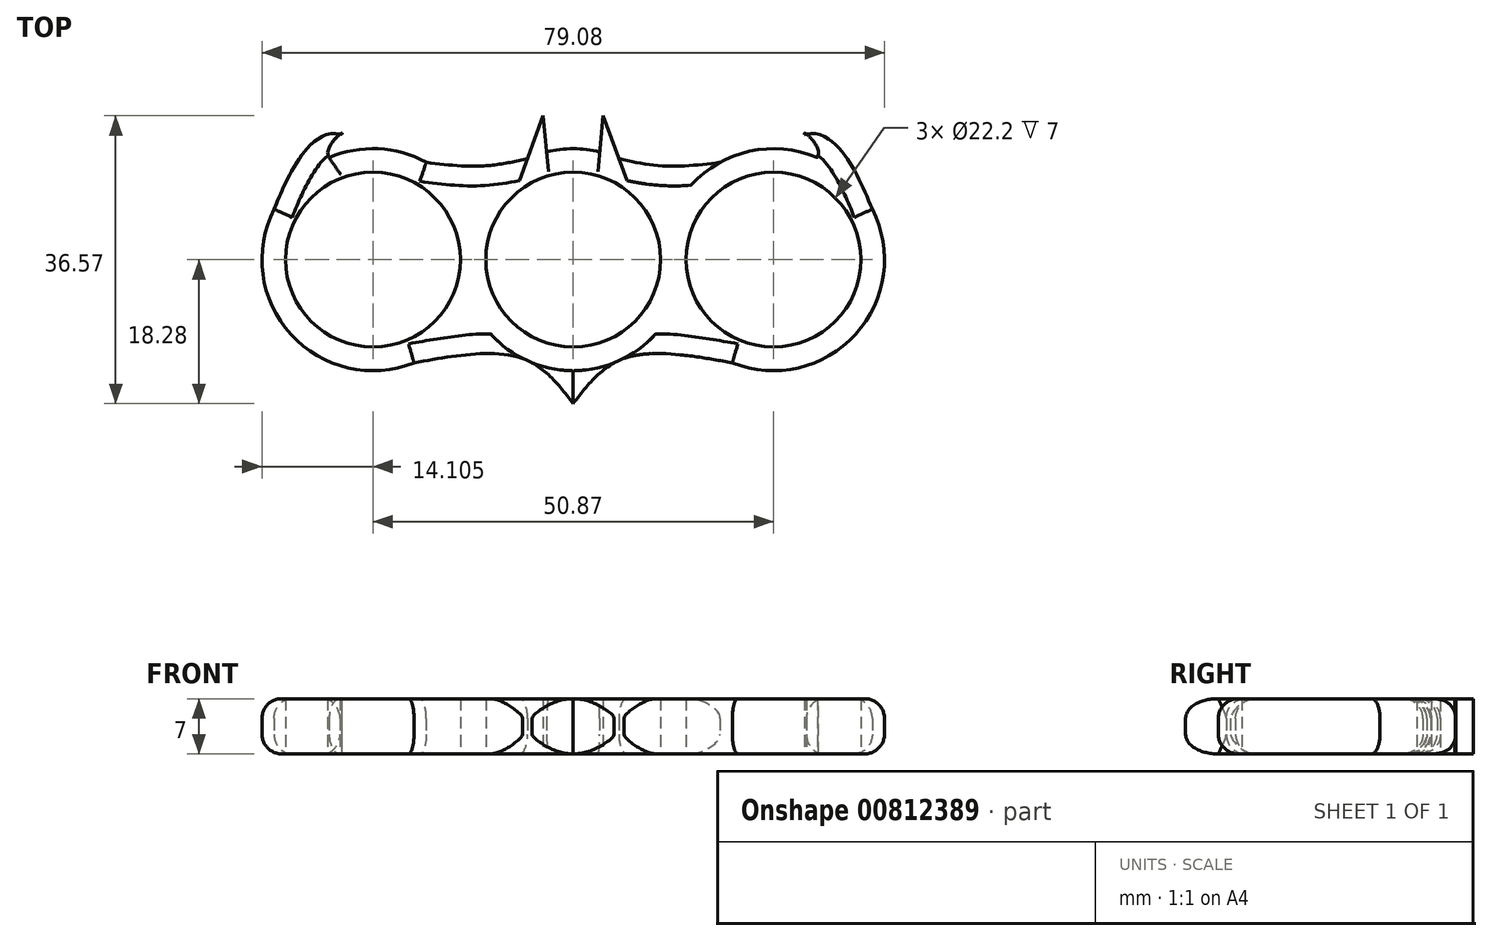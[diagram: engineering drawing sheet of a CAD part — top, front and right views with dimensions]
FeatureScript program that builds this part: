
annotation { "Feature Type Name" : "Feature", "Feature Type Description" : "" }
export const myFeature = defineFeature(function(context is Context, id is Id, definition is map)
    precondition{}
    {
        {
            var Q0;
            Q0=qCreatedBy(makeId("Top.planeOp"),FACE);
            var sketch = newSketch(context, id + "F0", { "sketchPlane" : qUnion([Q0])});
            skCircle(sketch, "E0", {"center": v(0, 0) * mm, "radius": 11.1 * mm});
            skCircle(sketch, "E1", {"center": v(0, 0) * mm, "radius": 14.1 * mm});
            skLineSegment(sketch, "E2", {"start": v(-3.37, 13.7) * mm, "end": v(-3.8, 18.3) * mm});
            skLineSegment(sketch, "E3", {"start": v(-3.8, 18.3) * mm, "end": v(-5.79, 12.86) * mm});
            skCircle(sketch, "E4", {"center": v(-25.44, 0) * mm, "radius": 11.1 * mm});
            skCircle(sketch, "E5", {"center": v(-25.44, 0) * mm, "radius": 14.1 * mm});
            skFitSpline(sketch, "E6", {"points": [v(-5.79, 12.86) * mm, v(-18.67, 12.37) * mm], "startDerivative": vector(-16.12, -4.1) * mm, "endDerivative": vector(-14.26, 1.86) * mm});
            skFitSpline(sketch, "E7", {"points": [v(-31, 12.95) * mm, v(-29.4, 15.9) * mm], "startDerivative": vector(-2.6, 3.82) * mm, "endDerivative": vector(-1.29, -2.38) * mm});
            skFitSpline(sketch, "E8", {"points": [v(-29.4, 15.9) * mm, v(-38.8, 4.5) * mm], "startDerivative": vector(-14.93, 3.99) * mm, "endDerivative": vector(-3.9, -8.33) * mm});
            skFitSpline(sketch, "E9", {"points": [v(-20.22, -13.1) * mm, v(-6.43, -12.55) * mm, v(0, -18.28) * mm], "startDerivative": vector(27.44, 4.82) * mm, "endDerivative": vector(12.4, -15.93) * mm});
            skLineSegment(sketch, "E10", {"start": v(0, 14.1) * mm, "end": v(0, -18.28) * mm, "construction": true});
            skLineSegment(sketch, "E11.MirrorCS", {"start": v(3.8, 18.3) * mm, "end": v(5.79, 12.86) * mm});
            skLineSegment(sketch, "E12.MirrorCS", {"start": v(3.37, 13.7) * mm, "end": v(3.8, 18.3) * mm});
            skFitSpline(sketch, "E13.MirrorCS", {"points": [v(5.79, 12.86) * mm, v(18.67, 12.37) * mm], "startDerivative": vector(16.12, -4.1) * mm, "endDerivative": vector(14.26, 1.86) * mm});
            skCircle(sketch, "E14.MirrorC", {"center": v(25.44, 0) * mm, "radius": 11.1 * mm});
            skCircle(sketch, "E15.MirrorC", {"center": v(25.44, 0) * mm, "radius": 14.1 * mm});
            skFitSpline(sketch, "E16.MirrorCS", {"points": [v(20.22, -13.1) * mm, v(6.43, -12.55) * mm, v(0, -18.28) * mm], "startDerivative": vector(-27.44, 4.82) * mm, "endDerivative": vector(-12.4, -15.93) * mm});
            skFitSpline(sketch, "E17.MirrorCS", {"points": [v(29.4, 15.9) * mm, v(38.8, 4.5) * mm], "startDerivative": vector(14.93, 3.99) * mm, "endDerivative": vector(3.9, -8.33) * mm});
            skFitSpline(sketch, "E18.MirrorCS", {"points": [v(31, 12.95) * mm, v(29.4, 15.9) * mm], "startDerivative": vector(2.6, 3.82) * mm, "endDerivative": vector(1.29, -2.38) * mm});
            skLineSegment(sketch, "E19.MirrorCS", {"start": v(34.7, 6.12) * mm, "end": v(29.4, 15.9) * mm, "construction": true});
            skSolve(sketch);
        }
        {
            var Q0;
            Q0 = qSketchRegion(id + "F0", true);
            var Q1;
            {var subQ0=sQuery(id+"F0.wireOp",EDGE,"E15.MirrorC");var subQ1=sQuery(id+"F0.wireOp",EDGE,"E1");var subQ2=makeQuery(id+"F0.imprint","INTERSECT",VERTEX,{"disambiguationData":[OD(0.0)],"derivedFrom":[subQ1,subQ0]});Q1=makeQuery(id+"F0.imprint","IMPRINT",FACE,{"disambiguationData":[TD([[makeQuery(id+"F0.imprint","IMPRINT",EDGE,{"disambiguationData":[TD([[subQ2,1.0]])],"derivedFrom":subQ1}),1.0]])]});}
            var Q2;
            {var subQ0=sQuery(id+"F0.wireOp",EDGE,"E5");var subQ1=sQuery(id+"F0.wireOp",EDGE,"E1");var subQ2=makeQuery(id+"F0.imprint","INTERSECT",VERTEX,{"disambiguationData":[OD(0.0)],"derivedFrom":[subQ1,subQ0]});Q2=makeQuery(id+"F0.imprint","IMPRINT",FACE,{"disambiguationData":[TD([[makeQuery(id+"F0.imprint","IMPRINT",EDGE,{"disambiguationData":[TD([[subQ2,-1.0]])],"derivedFrom":subQ1}),1.0]])]});}
            extrude(context, id + "F1", {"entities" : qUnion([Q0, Q1, Q2]), "depth" : 7 * mm, "offsetDistance" : 25 * mm});
        }
        {
            var Q0;
            {var subQ0=sQuery(id+"F0.wireOp",EDGE,"E5");Q0=makeQuery(id+"F1.opExtrude","CAP_EDGE",EDGE,{"disambiguationData":[OSD([subQ0]),TDD([makeQuery(id+"F0.imprint","IMPRINT",EDGE,{"disambiguationData":[TD([[makeQuery(id+"F0.imprint","INTERSECT",VERTEX,{"derivedFrom":[subQ0,sQuery(id+"F0.wireOp",EDGE,"E6")]}),-1.0]])],"derivedFrom":subQ0})])],"isStart":false});}
            var Q1;
            Q1=makeQuery(id+"F1.opExtrude","CAP_EDGE",EDGE,{"disambiguationData":[OSD([sQuery(id+"F0.wireOp",EDGE,"E6")])],"isStart":false});
            var Q2;
            {var subQ0=sQuery(id+"F0.wireOp",EDGE,"E8");Q2=makeQuery(id+"F1.opExtrude","CAP_EDGE",EDGE,{"disambiguationData":[OSD([subQ0]),TDD([makeQuery(id+"F0.imprint","IMPRINT",EDGE,{"disambiguationData":[TD([[makeQuery(id+"F0.imprint","INTERSECT",VERTEX,{"disambiguationData":[OD(1.0)],"derivedFrom":[sQuery(id+"F0.wireOp",EDGE,"E7"),subQ0]}),-1.0]])],"derivedFrom":subQ0})])],"isStart":false});}
            var Q3;
            {var subQ0=sQuery(id+"F0.wireOp",EDGE,"E8");var subQ1=sQuery(id+"F0.wireOp",EDGE,"E5");var subQ2=makeQuery(id+"F0.imprint","INTERSECT",VERTEX,{"disambiguationData":[OD(0.0)],"derivedFrom":[subQ1,subQ0]});Q3=makeQuery(id+"F1.opExtrude","CAP_EDGE",EDGE,{"disambiguationData":[OSD([subQ1]),TDD([makeQuery(id+"F0.imprint","IMPRINT",EDGE,{"disambiguationData":[TD([[subQ2,1.0]])],"derivedFrom":subQ1}),makeQuery(id+"F0.imprint","IMPRINT",EDGE,{"disambiguationData":[TD([[subQ2,-1.0]])],"derivedFrom":subQ1})])],"isStart":false});}
            var Q4;
            {var subQ0=sQuery(id+"F0.wireOp",EDGE,"E9");Q4=makeQuery(id+"F1.opExtrude","CAP_EDGE",EDGE,{"disambiguationData":[OSD([subQ0]),TDD([makeQuery(id+"F0.imprint","IMPRINT",EDGE,{"disambiguationData":[TD([[makeQuery(id+"F0.imprint","INTERSECT",VERTEX,{"derivedFrom":[sQuery(id+"F0.wireOp",EDGE,"E5"),subQ0]}),-1.0]])],"derivedFrom":subQ0})])],"isStart":false});}
            var Q5;
            {var subQ0=sQuery(id+"F0.wireOp",EDGE,"E9");Q5=makeQuery(id+"F1.opExtrude","CAP_EDGE",EDGE,{"disambiguationData":[OSD([subQ0]),TDD([makeQuery(id+"F0.imprint","IMPRINT",EDGE,{"disambiguationData":[TD([[makeQuery(id+"F0.imprint","INTERSECT",VERTEX,{"derivedFrom":[subQ0,sQuery(id+"F0.wireOp",EDGE,"E16.MirrorCS")]}),1.0]])],"derivedFrom":subQ0})])],"isStart":false});}
            var Q6;
            {var subQ0=sQuery(id+"F0.wireOp",EDGE,"E16.MirrorCS");Q6=makeQuery(id+"F1.opExtrude","CAP_EDGE",EDGE,{"disambiguationData":[OSD([subQ0]),TDD([makeQuery(id+"F0.imprint","IMPRINT",EDGE,{"disambiguationData":[TD([[makeQuery(id+"F0.imprint","INTERSECT",VERTEX,{"derivedFrom":[sQuery(id+"F0.wireOp",EDGE,"E15.MirrorC"),subQ0]}),-1.0]])],"derivedFrom":subQ0})])],"isStart":false});}
            var Q7;
            {var subQ0=sQuery(id+"F0.wireOp",EDGE,"E16.MirrorCS");Q7=makeQuery(id+"F1.opExtrude","CAP_EDGE",EDGE,{"disambiguationData":[OSD([subQ0]),TDD([makeQuery(id+"F0.imprint","IMPRINT",EDGE,{"disambiguationData":[TD([[makeQuery(id+"F0.imprint","INTERSECT",VERTEX,{"derivedFrom":[sQuery(id+"F0.wireOp",EDGE,"E9"),subQ0]}),1.0]])],"derivedFrom":subQ0})])],"isStart":false});}
            var Q8;
            {var subQ0=sQuery(id+"F0.wireOp",EDGE,"E15.MirrorC");var subQ1=sQuery(id+"F0.wireOp",EDGE,"E17.MirrorCS");var subQ2=makeQuery(id+"F0.imprint","INTERSECT",VERTEX,{"disambiguationData":[OD(0.0)],"derivedFrom":[subQ0,subQ1]});Q8=makeQuery(id+"F1.opExtrude","CAP_EDGE",EDGE,{"disambiguationData":[OSD([subQ0]),TDD([makeQuery(id+"F0.imprint","IMPRINT",EDGE,{"disambiguationData":[TD([[subQ2,1.0]])],"derivedFrom":subQ0}),makeQuery(id+"F0.imprint","IMPRINT",EDGE,{"disambiguationData":[TD([[makeQuery(id+"F0.imprint","INTERSECT",VERTEX,{"derivedFrom":[subQ0,sQuery(id+"F0.wireOp",EDGE,"E16.MirrorCS")]}),1.0]])],"derivedFrom":subQ0})])],"isStart":false});}
            var Q9;
            {var subQ0=sQuery(id+"F0.wireOp",EDGE,"E17.MirrorCS");Q9=makeQuery(id+"F1.opExtrude","CAP_EDGE",EDGE,{"disambiguationData":[OSD([subQ0]),TDD([makeQuery(id+"F0.imprint","IMPRINT",EDGE,{"disambiguationData":[TD([[makeQuery(id+"F0.imprint","INTERSECT",VERTEX,{"disambiguationData":[OD(1.0)],"derivedFrom":[subQ0,sQuery(id+"F0.wireOp",EDGE,"E18.MirrorCS")]}),-1.0]])],"derivedFrom":subQ0})])],"isStart":false});}
            var Q10;
            {var subQ0=sQuery(id+"F0.wireOp",EDGE,"E15.MirrorC");Q10=makeQuery(id+"F1.opExtrude","CAP_EDGE",EDGE,{"disambiguationData":[OSD([subQ0]),TDD([makeQuery(id+"F0.imprint","IMPRINT",EDGE,{"disambiguationData":[TD([[makeQuery(id+"F0.imprint","INTERSECT",VERTEX,{"derivedFrom":[sQuery(id+"F0.wireOp",EDGE,"E13.MirrorCS"),subQ0]}),-1.0]])],"derivedFrom":subQ0})])],"isStart":false});}
            var Q11;
            Q11=makeQuery(id+"F1.opExtrude","CAP_EDGE",EDGE,{"disambiguationData":[OSD([sQuery(id+"F0.wireOp",EDGE,"E13.MirrorCS")])],"isStart":false});
            var Q12;
            {var subQ0=sQuery(id+"F0.wireOp",EDGE,"E1");Q12=makeQuery(id+"F1.opExtrude","CAP_EDGE",EDGE,{"disambiguationData":[OSD([subQ0]),TDD([makeQuery(id+"F0.imprint","IMPRINT",EDGE,{"disambiguationData":[TD([[makeQuery(id+"F0.imprint","INTERSECT",VERTEX,{"derivedFrom":[subQ0,sQuery(id+"F0.wireOp",EDGE,"E2")]}),1.0]])],"derivedFrom":subQ0})])],"isStart":false});}
            var Q13;
            {var subQ0=sQuery(id+"F0.wireOp",EDGE,"E8");var subQ1=sQuery(id+"F0.wireOp",EDGE,"E5");var subQ2=makeQuery(id+"F0.imprint","INTERSECT",VERTEX,{"disambiguationData":[OD(0.0)],"derivedFrom":[subQ1,subQ0]});Q13=makeQuery(id+"F1.opExtrude","CAP_EDGE",EDGE,{"disambiguationData":[OSD([subQ1]),TDD([makeQuery(id+"F0.imprint","IMPRINT",EDGE,{"disambiguationData":[TD([[subQ2,1.0]])],"derivedFrom":subQ1}),makeQuery(id+"F0.imprint","IMPRINT",EDGE,{"disambiguationData":[TD([[subQ2,-1.0]])],"derivedFrom":subQ1})])],"isStart":true});}
            var Q14;
            {var subQ0=sQuery(id+"F0.wireOp",EDGE,"E8");Q14=makeQuery(id+"F1.opExtrude","CAP_EDGE",EDGE,{"disambiguationData":[OSD([subQ0]),TDD([makeQuery(id+"F0.imprint","IMPRINT",EDGE,{"disambiguationData":[TD([[makeQuery(id+"F0.imprint","INTERSECT",VERTEX,{"disambiguationData":[OD(1.0)],"derivedFrom":[sQuery(id+"F0.wireOp",EDGE,"E7"),subQ0]}),-1.0]])],"derivedFrom":subQ0})])],"isStart":true});}
            var Q15;
            Q15=makeQuery(id+"F1.opExtrude","CAP_EDGE",EDGE,{"disambiguationData":[OSD([sQuery(id+"F0.wireOp",EDGE,"E6")])],"isStart":true});
            var Q16;
            {var subQ0=sQuery(id+"F0.wireOp",EDGE,"E5");Q16=makeQuery(id+"F1.opExtrude","CAP_EDGE",EDGE,{"disambiguationData":[OSD([subQ0]),TDD([makeQuery(id+"F0.imprint","IMPRINT",EDGE,{"disambiguationData":[TD([[makeQuery(id+"F0.imprint","INTERSECT",VERTEX,{"derivedFrom":[subQ0,sQuery(id+"F0.wireOp",EDGE,"E6")]}),-1.0]])],"derivedFrom":subQ0})])],"isStart":true});}
            var Q17;
            {var subQ0=sQuery(id+"F0.wireOp",EDGE,"E1");Q17=makeQuery(id+"F1.opExtrude","CAP_EDGE",EDGE,{"disambiguationData":[OSD([subQ0]),TDD([makeQuery(id+"F0.imprint","IMPRINT",EDGE,{"disambiguationData":[TD([[makeQuery(id+"F0.imprint","INTERSECT",VERTEX,{"derivedFrom":[subQ0,sQuery(id+"F0.wireOp",EDGE,"E2")]}),1.0]])],"derivedFrom":subQ0})])],"isStart":true});}
            var Q18;
            Q18=makeQuery(id+"F1.opExtrude","CAP_EDGE",EDGE,{"disambiguationData":[OSD([sQuery(id+"F0.wireOp",EDGE,"E13.MirrorCS")])],"isStart":true});
            var Q19;
            {var subQ0=sQuery(id+"F0.wireOp",EDGE,"E15.MirrorC");Q19=makeQuery(id+"F1.opExtrude","CAP_EDGE",EDGE,{"disambiguationData":[OSD([subQ0]),TDD([makeQuery(id+"F0.imprint","IMPRINT",EDGE,{"disambiguationData":[TD([[makeQuery(id+"F0.imprint","INTERSECT",VERTEX,{"derivedFrom":[sQuery(id+"F0.wireOp",EDGE,"E13.MirrorCS"),subQ0]}),-1.0]])],"derivedFrom":subQ0})])],"isStart":true});}
            var Q20;
            {var subQ0=sQuery(id+"F0.wireOp",EDGE,"E17.MirrorCS");Q20=makeQuery(id+"F1.opExtrude","CAP_EDGE",EDGE,{"disambiguationData":[OSD([subQ0]),TDD([makeQuery(id+"F0.imprint","IMPRINT",EDGE,{"disambiguationData":[TD([[makeQuery(id+"F0.imprint","INTERSECT",VERTEX,{"disambiguationData":[OD(1.0)],"derivedFrom":[subQ0,sQuery(id+"F0.wireOp",EDGE,"E18.MirrorCS")]}),-1.0]])],"derivedFrom":subQ0})])],"isStart":true});}
            var Q21;
            {var subQ0=sQuery(id+"F0.wireOp",EDGE,"E15.MirrorC");var subQ1=sQuery(id+"F0.wireOp",EDGE,"E17.MirrorCS");var subQ2=makeQuery(id+"F0.imprint","INTERSECT",VERTEX,{"disambiguationData":[OD(0.0)],"derivedFrom":[subQ0,subQ1]});Q21=makeQuery(id+"F1.opExtrude","CAP_EDGE",EDGE,{"disambiguationData":[OSD([subQ0]),TDD([makeQuery(id+"F0.imprint","IMPRINT",EDGE,{"disambiguationData":[TD([[subQ2,1.0]])],"derivedFrom":subQ0}),makeQuery(id+"F0.imprint","IMPRINT",EDGE,{"disambiguationData":[TD([[makeQuery(id+"F0.imprint","INTERSECT",VERTEX,{"derivedFrom":[subQ0,sQuery(id+"F0.wireOp",EDGE,"E16.MirrorCS")]}),1.0]])],"derivedFrom":subQ0})])],"isStart":true});}
            var Q22;
            {var subQ0=sQuery(id+"F0.wireOp",EDGE,"E16.MirrorCS");Q22=makeQuery(id+"F1.opExtrude","CAP_EDGE",EDGE,{"disambiguationData":[OSD([subQ0]),TDD([makeQuery(id+"F0.imprint","IMPRINT",EDGE,{"disambiguationData":[TD([[makeQuery(id+"F0.imprint","INTERSECT",VERTEX,{"derivedFrom":[sQuery(id+"F0.wireOp",EDGE,"E15.MirrorC"),subQ0]}),-1.0]])],"derivedFrom":subQ0})])],"isStart":true});}
            var Q23;
            {var subQ0=sQuery(id+"F0.wireOp",EDGE,"E16.MirrorCS");Q23=makeQuery(id+"F1.opExtrude","CAP_EDGE",EDGE,{"disambiguationData":[OSD([subQ0]),TDD([makeQuery(id+"F0.imprint","IMPRINT",EDGE,{"disambiguationData":[TD([[makeQuery(id+"F0.imprint","INTERSECT",VERTEX,{"derivedFrom":[sQuery(id+"F0.wireOp",EDGE,"E9"),subQ0]}),1.0]])],"derivedFrom":subQ0})])],"isStart":true});}
            var Q24;
            {var subQ0=sQuery(id+"F0.wireOp",EDGE,"E9");Q24=makeQuery(id+"F1.opExtrude","CAP_EDGE",EDGE,{"disambiguationData":[OSD([subQ0]),TDD([makeQuery(id+"F0.imprint","IMPRINT",EDGE,{"disambiguationData":[TD([[makeQuery(id+"F0.imprint","INTERSECT",VERTEX,{"derivedFrom":[sQuery(id+"F0.wireOp",EDGE,"E5"),subQ0]}),-1.0]])],"derivedFrom":subQ0})])],"isStart":true});}
            var Q25;
            {var subQ0=sQuery(id+"F0.wireOp",EDGE,"E9");Q25=makeQuery(id+"F1.opExtrude","CAP_EDGE",EDGE,{"disambiguationData":[OSD([subQ0]),TDD([makeQuery(id+"F0.imprint","IMPRINT",EDGE,{"disambiguationData":[TD([[makeQuery(id+"F0.imprint","INTERSECT",VERTEX,{"derivedFrom":[subQ0,sQuery(id+"F0.wireOp",EDGE,"E16.MirrorCS")]}),1.0]])],"derivedFrom":subQ0})])],"isStart":true});}
            fillet(context, id + "F2", {"entities" : qUnion([Q0, Q1, Q2, Q3, Q4, Q5, Q6, Q7, Q8, Q9, Q10, Q11, Q12, Q13, Q14, Q15, Q16, Q17, Q18, Q19, Q20, Q21, Q22, Q23, Q24, Q25]), "radius" : 2.5 * mm, "tangentPropagation" : true, "allowEdgeOverflow" : false});
        }
    });
